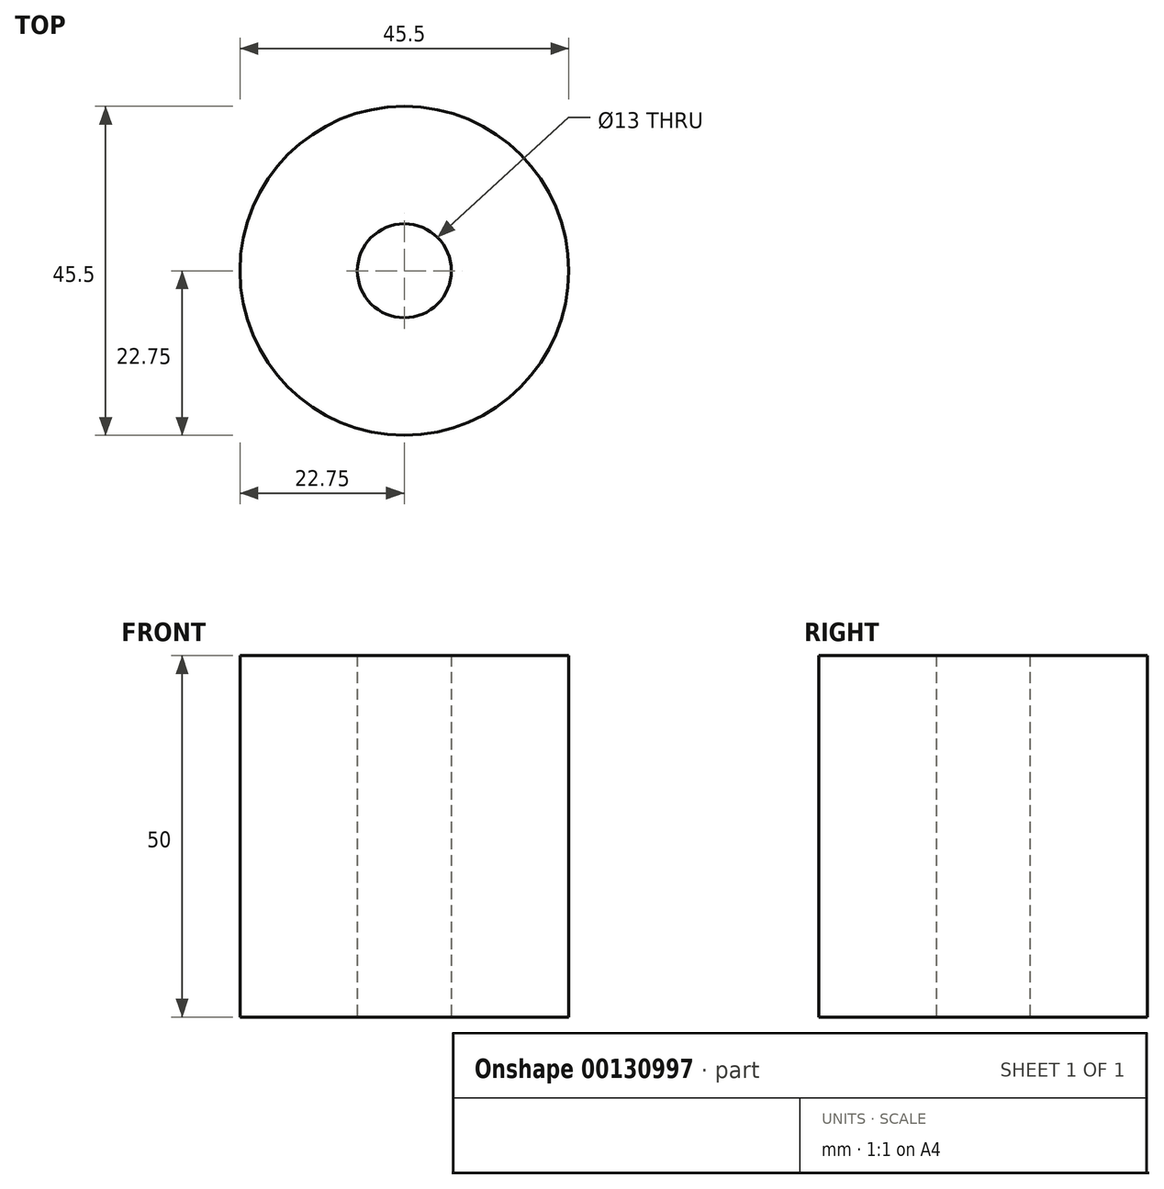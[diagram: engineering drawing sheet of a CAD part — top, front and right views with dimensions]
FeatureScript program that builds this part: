
annotation { "Feature Type Name" : "Feature", "Feature Type Description" : "" }
export const myFeature = defineFeature(function(context is Context, id is Id, definition is map)
    precondition{}
    {
        {
            var Q0;
            Q0=qCreatedBy(makeId("Top.planeOp"),FACE);
            var sketch = newSketch(context, id + "F0", { "sketchPlane" : qUnion([Q0])});
            skCircle(sketch, "E0", {"center": v(0, 0) * mm, "radius": 22.75 * mm});
            skCircle(sketch, "E1", {"center": v(0, 0) * mm, "radius": 6.5 * mm});
            skSolve(sketch);
        }
        {
            var Q0;
            Q0=makeQuery(id+"F0.imprint","IMPRINT",FACE,{"disambiguationData":[TD([[makeQuery(id+"F0.imprint","IMPRINT",EDGE,{"derivedFrom":sQuery(id+"F0.wireOp",EDGE,"E0")}),1.0]])]});
            extrude(context, id + "F1", {"entities" : qUnion([Q0]), "depth" : 50 * mm});
        }
    });
